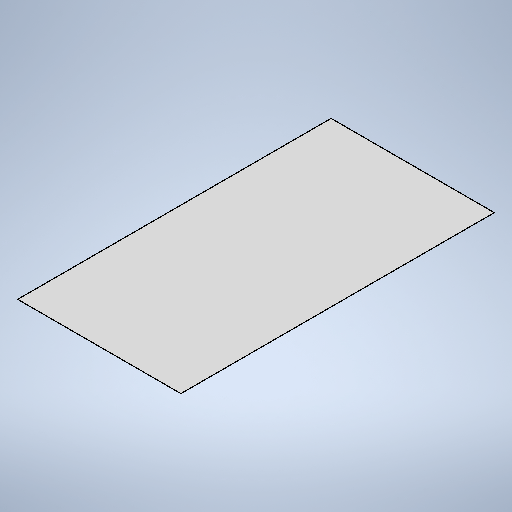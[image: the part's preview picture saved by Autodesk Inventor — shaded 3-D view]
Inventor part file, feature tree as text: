
AUTODESK INVENTOR PART (.ipt)
format: ipt  version: 2025 (Build 290162010, 162A)  size: 260,608 bytes
history: native  units: mm
features: sheet_metal_op x1, sketch x1, other x1
ambient origin geometry x8: Origin, YZ Plane, XZ Plane, XY Plane, X Axis, Y Axis, Z Axis, Center Point
bodies: Body1 (feature_tree)
feature tree (3):
  sheet_metal_op  "Face3"
  sketch  "Sketch1"  dims[d61=500.0mm d154=1250.0mm d155=2400.0mm d156=2.0mm]
  other  "Plate5"
